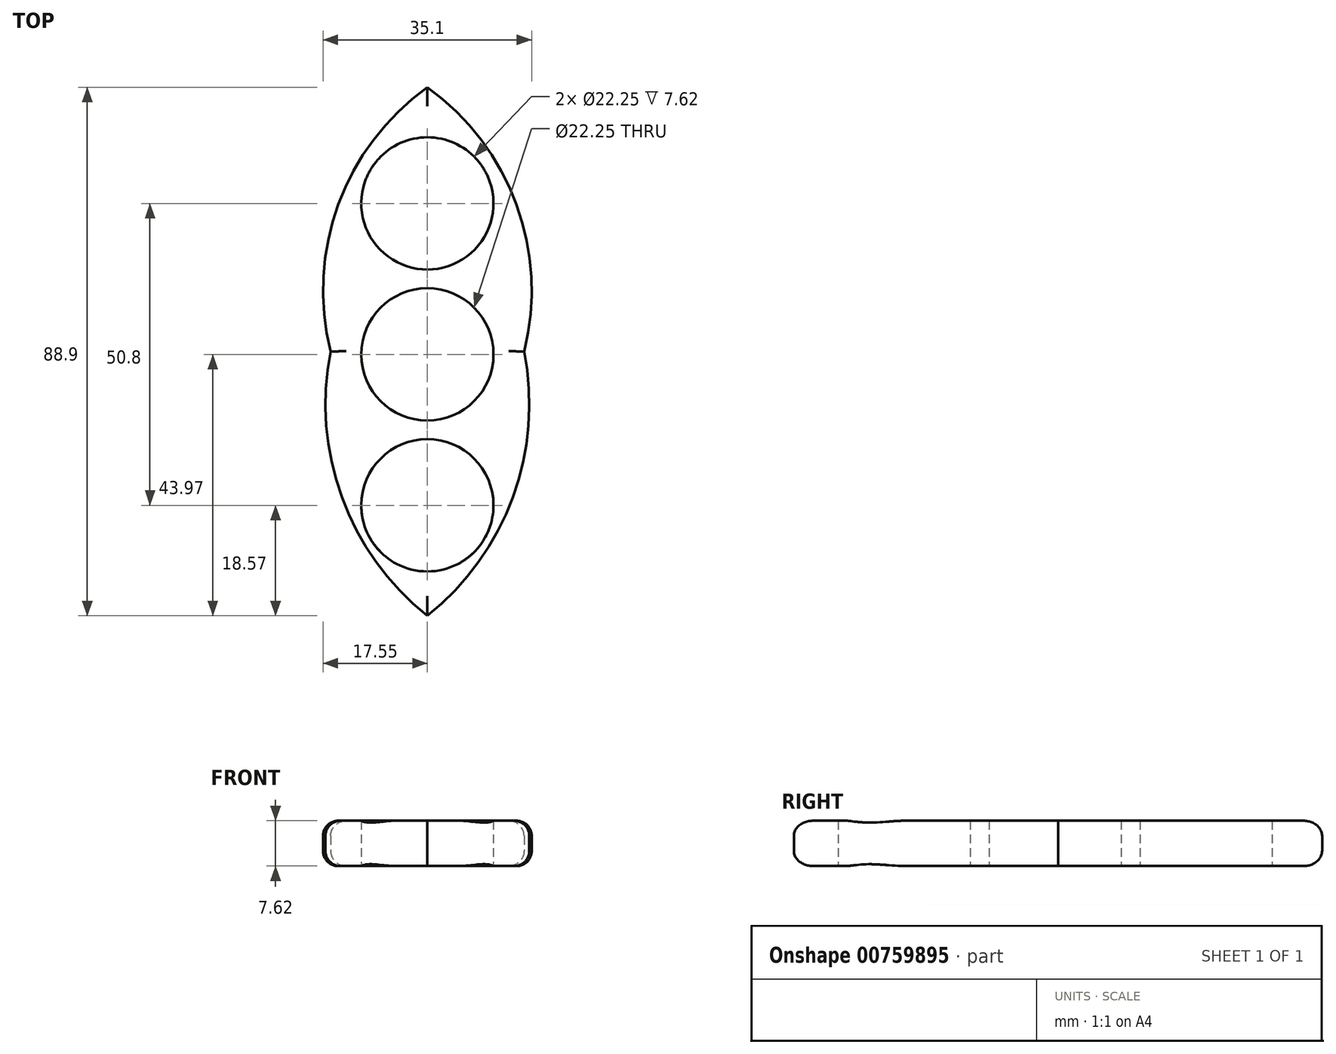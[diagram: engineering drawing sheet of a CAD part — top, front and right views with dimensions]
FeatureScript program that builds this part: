
annotation { "Feature Type Name" : "Feature", "Feature Type Description" : "" }
export const myFeature = defineFeature(function(context is Context, id is Id, definition is map)
    precondition{}
    {
        {
            var Q0;
            Q0=qCreatedBy(makeId("Top.planeOp"),FACE);
            var sketch = newSketch(context, id + "F0", { "sketchPlane" : qUnion([Q0])});
            skCircle(sketch, "E0", {"center": v(0, 0) * mm, "radius": 11.13 * mm});
            skCircle(sketch, "E1", {"center": v(0, -25.4) * mm, "radius": 11.13 * mm});
            skCircle(sketch, "E2", {"center": v(0, 25.4) * mm, "radius": 11.13 * mm});
            skArc(sketch, "E3", {"start": v(0, 44.93) * mm, "mid": v(-14.99, 25.22) * mm, "end": v(-16.27, 0.48) * mm});
            skPoint(sketch, "E3.endSnap0", {"position": v(0, 0.48) * mm});
            skArc(sketch, "E4", {"start": v(-16.27, 0.48) * mm, "mid": v(-14.39, -24.03) * mm, "end": v(0, -43.97) * mm});
            skArc(sketch, "E5.MirrorCS", {"start": v(16.27, 0.48) * mm, "mid": v(14.39, -24.03) * mm, "end": v(0, -43.97) * mm});
            skArc(sketch, "E6.MirrorCS", {"start": v(0, 44.93) * mm, "mid": v(14.99, 25.22) * mm, "end": v(16.27, 0.48) * mm});
            skSolve(sketch);
        }
        {
            var Q0;
            Q0=makeQuery(id+"F0.imprint","IMPRINT",FACE,{"disambiguationData":[TD([[makeQuery(id+"F0.imprint","IMPRINT",EDGE,{"derivedFrom":sQuery(id+"F0.wireOp",EDGE,"E0")}),-1.0]])]});
            extrude(context, id + "F1", {"entities" : qUnion([Q0]), "endBound" : BoundingType.SYMMETRIC, "depth" : 7.62 * mm, "offsetDistance" : 25.4 * mm});
        }
        {
            var Q0;
            Q0=makeQuery(id+"F1.opExtrude","CAP_EDGE",EDGE,{"disambiguationData":[OSD([sQuery(id+"F0.wireOp",EDGE,"E5.MirrorCS")])],"isStart":false});
            var Q1;
            Q1=makeQuery(id+"F1.opExtrude","CAP_EDGE",EDGE,{"disambiguationData":[OSD([sQuery(id+"F0.wireOp",EDGE,"E5.MirrorCS")])],"isStart":true});
            var Q2;
            Q2=makeQuery(id+"F1.opExtrude","CAP_EDGE",EDGE,{"disambiguationData":[OSD([sQuery(id+"F0.wireOp",EDGE,"E6.MirrorCS")])],"isStart":false});
            var Q3;
            Q3=makeQuery(id+"F1.opExtrude","CAP_EDGE",EDGE,{"disambiguationData":[OSD([sQuery(id+"F0.wireOp",EDGE,"E6.MirrorCS")])],"isStart":true});
            var Q4;
            Q4=makeQuery(id+"F1.opExtrude","CAP_EDGE",EDGE,{"disambiguationData":[OSD([sQuery(id+"F0.wireOp",EDGE,"E4")])],"isStart":false});
            var Q5;
            Q5=makeQuery(id+"F1.opExtrude","CAP_EDGE",EDGE,{"disambiguationData":[OSD([sQuery(id+"F0.wireOp",EDGE,"E4")])],"isStart":true});
            var Q6;
            Q6=makeQuery(id+"F1.opExtrude","CAP_EDGE",EDGE,{"disambiguationData":[OSD([sQuery(id+"F0.wireOp",EDGE,"E3")])],"isStart":false});
            var Q7;
            Q7=makeQuery(id+"F1.opExtrude","CAP_EDGE",EDGE,{"disambiguationData":[OSD([sQuery(id+"F0.wireOp",EDGE,"E3")])],"isStart":true});
            fillet(context, id + "F2", {"entities" : qUnion([Q0, Q1, Q2, Q3, Q4, Q5, Q6, Q7]), "radius" : 2.54 * mm, "tangentPropagation" : true, "allowEdgeOverflow" : false});
        }
    });
